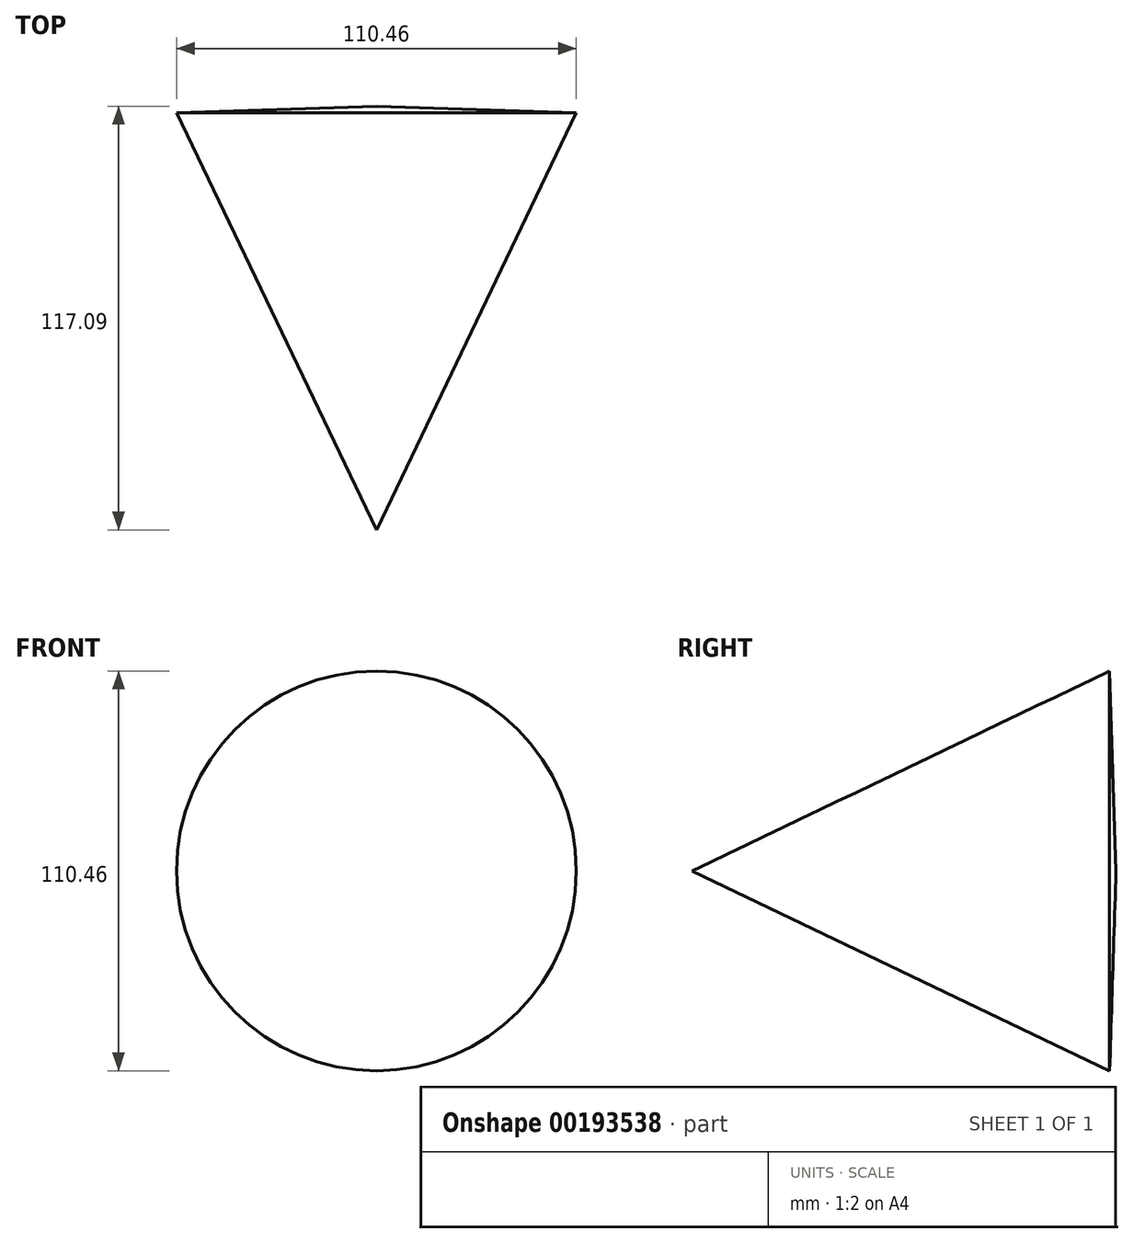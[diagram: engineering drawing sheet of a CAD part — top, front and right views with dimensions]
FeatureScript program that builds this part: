
annotation { "Feature Type Name" : "Feature", "Feature Type Description" : "" }
export const myFeature = defineFeature(function(context is Context, id is Id, definition is map)
    precondition{}
    {
        {
            var Q0;
            Q0=qCreatedBy(makeId("Top.planeOp"),FACE);
            var sketch = newSketch(context, id + "F0", { "sketchPlane" : qUnion([Q0])});
            skLineSegment(sketch, "E0", {"start": v(0, 56.78) * mm, "end": v(0, -60.31) * mm});
            skLineSegment(sketch, "E1", {"start": v(0, -60.31) * mm, "end": v(55.23, 55.01) * mm});
            skLineSegment(sketch, "E2", {"start": v(55.23, 55.01) * mm, "end": v(0, 56.78) * mm});
            skSolve(sketch);
        }
        {
            var Q0;
            Q0=makeQuery(id+"F0.imprint","IMPRINT",FACE,{"disambiguationData":[TD([[makeQuery(id+"F0.imprint","IMPRINT",EDGE,{"derivedFrom":sQuery(id+"F0.wireOp",EDGE,"E0")}),1.0]])]});
            var Q1;
            Q1=sQuery(id+"F0.wireOp",EDGE,"E0");
            revolve(context, id + "F1", {"entities" : qUnion([Q0]), "axis" : qUnion([Q1]), "revolveType" : RevolveType.FULL});
        }
    });
